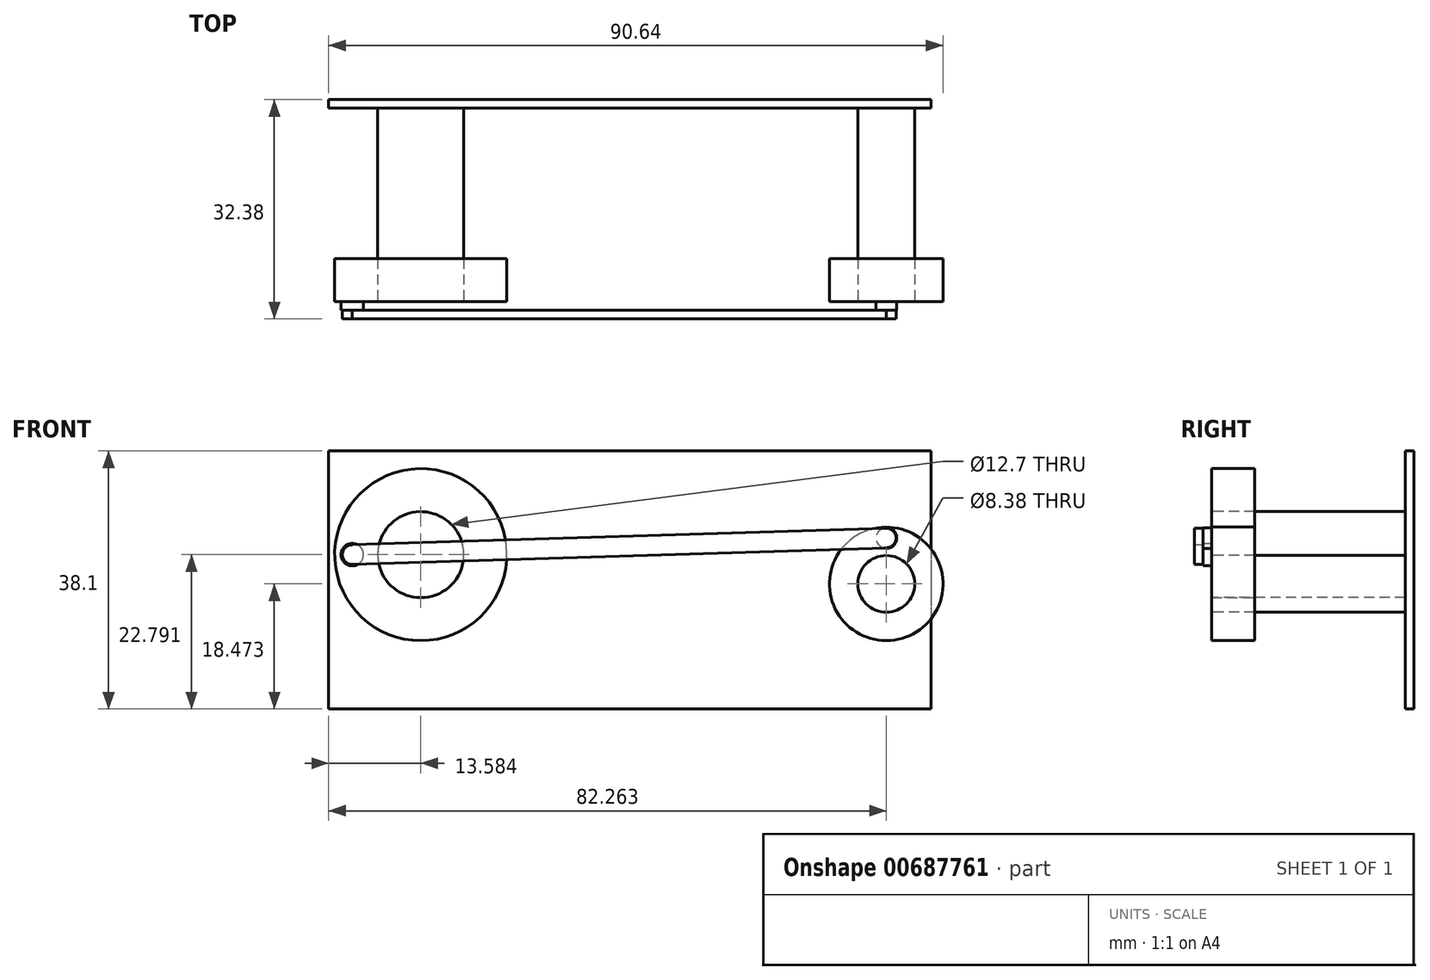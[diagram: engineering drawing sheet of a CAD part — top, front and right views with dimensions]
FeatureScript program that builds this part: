
annotation { "Feature Type Name" : "Feature", "Feature Type Description" : "" }
export const myFeature = defineFeature(function(context is Context, id is Id, definition is map)
    precondition{}
    {
        {
            var Q0;
            Q0=qCreatedBy(makeId("Front.planeOp"),FACE);
            var sketch = newSketch(context, id + "F0", { "sketchPlane" : qUnion([Q0])});
            skCircle(sketch, "E0", {"center": v(-75.94, -5.97) * mm, "radius": 12.7 * mm});
            skCircle(sketch, "E1", {"center": v(-7.26, -10.29) * mm, "radius": 8.38 * mm});
            skCircle(sketch, "E2", {"center": v(-75.94, -5.97) * mm, "radius": 6.35 * mm});
            skCircle(sketch, "E3", {"center": v(-7.26, -10.29) * mm, "radius": 4.2 * mm});
            skSolve(sketch);
        }
        {
            var Q0;
            Q0=makeQuery(id+"F0.imprint","IMPRINT",FACE,{"disambiguationData":[TD([[makeQuery(id+"F0.imprint","IMPRINT",EDGE,{"derivedFrom":sQuery(id+"F0.wireOp",EDGE,"E0")}),1.0]])]});
            var Q1;
            Q1=makeQuery(id+"F0.imprint","IMPRINT",FACE,{"disambiguationData":[TD([[makeQuery(id+"F0.imprint","IMPRINT",EDGE,{"derivedFrom":sQuery(id+"F0.wireOp",EDGE,"E1")}),1.0]])]});
            extrude(context, id + "F1", {"entities" : qUnion([Q0, Q1]), "endBound" : BoundingType.SYMMETRIC, "depth" : 6.35 * mm, "offsetDistance" : 25.4 * mm});
        }
        {
            var Q0;
            Q0=makeQuery(id+"F0.imprint","IMPRINT",FACE,{"disambiguationData":[TD([[makeQuery(id+"F0.imprint","IMPRINT",EDGE,{"derivedFrom":sQuery(id+"F0.wireOp",EDGE,"E2")}),1.0]])]});
            var Q1;
            Q1=makeQuery(id+"F0.imprint","IMPRINT",FACE,{"disambiguationData":[TD([[makeQuery(id+"F0.imprint","IMPRINT",EDGE,{"derivedFrom":sQuery(id+"F0.wireOp",EDGE,"E3")}),1.0]])]});
            var Q2;
            Q2=makeQuery(id+"F1.opExtrude","CAP_FACE",FACE,{"disambiguationData":[OSD([sQuery(id+"F0.wireOp",EDGE,"E0"),sQuery(id+"F0.wireOp",EDGE,"E2")])],"isStart":false});
            extrude(context, id + "F2", {"entities" : qUnion([Q0, Q1]), "oppositeDirection" : true, "depth" : 25.4 * mm, "offsetDistance" : 25.4 * mm, "hasSecondDirection" : true, "secondDirectionBound" : SecondDirectionBoundingType.UP_TO_SURFACE, "secondDirectionOppositeDirection" : false, "secondDirectionDepth" : 25.4 * mm, "secondDirectionBoundEntityFace" : qUnion([Q2])});
        }
        {
            var Q0;
            Q0=makeQuery(id+"F2.opExtrude","CAP_FACE",FACE,{"disambiguationData":[OSD([sQuery(id+"F0.wireOp",EDGE,"E3")])],"isStart":false});
            var sketch = newSketch(context, id + "F3", { "sketchPlane" : qUnion([Q0])});
            skLineSegment(sketch, "E4.bottom", {"start": v(0.62, 9.34) * mm, "end": v(89.52, 9.34) * mm});
            skLineSegment(sketch, "E4.top", {"start": v(0.62, -28.76) * mm, "end": v(89.52, -28.76) * mm});
            skLineSegment(sketch, "E4.left", {"start": v(0.62, 9.34) * mm, "end": v(0.62, -28.76) * mm});
            skLineSegment(sketch, "E4.right", {"start": v(89.52, 9.34) * mm, "end": v(89.52, -28.76) * mm});
            skSolve(sketch);
        }
        {
            var Q0;
            Q0=makeQuery(id+"F3.imprint","IMPRINT",FACE,{"disambiguationData":[TD([[makeQuery(id+"F3.imprint","IMPRINT",EDGE,{"derivedFrom":sQuery(id+"F3.wireOp",EDGE,"E4.bottom")}),-1.0]])]});
            var Q1;
            Q1=makeQuery(id+"F3.imprint","IMPRINT",FACE,{"disambiguationData":[TD([[makeQuery(id+"F3.imprint","IMPRINT",EDGE,{"derivedFrom":makeQuery(id+"F2.opExtrude","CAP_EDGE",EDGE,{"disambiguationData":[OSD([sQuery(id+"F0.wireOp",EDGE,"E3")])],"isStart":false})}),-1.0]])]});
            extrude(context, id + "F4", {"entities" : qUnion([Q0, Q1]), "operationType" : NewBodyOperationType.ADD, "depth" : 1.27 * mm, "offsetDistance" : 25.4 * mm});
        }
        {
            var Q0;
            Q0=makeQuery(id+"F1.opExtrude","CAP_FACE",FACE,{"disambiguationData":[OSD([sQuery(id+"F0.wireOp",EDGE,"E0")])],"isStart":false});
            var sketch = newSketch(context, id + "F5", { "sketchPlane" : qUnion([Q0])});
            skPoint(sketch, "E5", {"position": v(-75.94, -5.97) * mm});
            skCircle(sketch, "E6", {"center": v(-86.04, -5.97) * mm, "radius": 1.46 * mm});
            skPoint(sketch, "E7", {"position": v(-7.22, -10.29) * mm});
            skCircle(sketch, "E8", {"center": v(-7.22, -3.5) * mm, "radius": 1.46 * mm});
            skCircle(sketch, "E9", {"center": v(-86.04, -5.97) * mm, "radius": 1.65 * mm});
            skCircle(sketch, "E10", {"center": v(-7.22, -3.5) * mm, "radius": 1.52 * mm});
            skSolve(sketch);
        }
        {
            var Q0;
            Q0=makeQuery(id+"F5.imprint","IMPRINT",FACE,{"disambiguationData":[TD([[makeQuery(id+"F5.imprint","IMPRINT",EDGE,{"derivedFrom":sQuery(id+"F5.wireOp",EDGE,"E6")}),1.0]])]});
            var Q1;
            Q1=makeQuery(id+"F5.imprint","IMPRINT",FACE,{"disambiguationData":[TD([[makeQuery(id+"F5.imprint","IMPRINT",EDGE,{"derivedFrom":sQuery(id+"F5.wireOp",EDGE,"E8")}),1.0]])]});
            extrude(context, id + "F6", {"entities" : qUnion([Q0, Q1]), "depth" : 1.27 * mm, "offsetDistance" : 25.4 * mm});
        }
        {
            var Q0;
            Q0=makeQuery(id+"F6.opExtrude","CAP_FACE",FACE,{"disambiguationData":[OSD([sQuery(id+"F5.wireOp",EDGE,"E6")])],"isStart":false});
            var sketch = newSketch(context, id + "F7", { "sketchPlane" : qUnion([Q0])});
            skPoint(sketch, "E11", {"position": v(-86.04, -5.97) * mm});
            skArc(sketch, "E12", {"start": v(-86.04, -4.5) * mm, "mid": v(-87.51, -5.97) * mm, "end": v(-86.04, -7.43) * mm});
            skLineSegment(sketch, "E13", {"start": v(-86.04, -4.5) * mm, "end": v(-7.23, -2.05) * mm});
            skLineSegment(sketch, "E14", {"start": v(-86.04, -7.43) * mm, "end": v(-7.23, -4.97) * mm});
            skArc(sketch, "E15", {"start": v(-7.23, -4.97) * mm, "mid": v(-5.8, -3.5) * mm, "end": v(-7.23, -2.05) * mm});
            skSolve(sketch);
        }
        {
            var Q0;
            Q0=makeQuery(id+"F5.imprint","IMPRINT",FACE,{"disambiguationData":[TD([[makeQuery(id+"F5.imprint","IMPRINT",EDGE,{"derivedFrom":sQuery(id+"F5.wireOp",EDGE,"E6")}),-1.0]])]});
            extrude(context, id + "F8", {"entities" : qUnion([Q0]), "operationType" : NewBodyOperationType.ADD, "depth" : 1.27 * mm, "offsetDistance" : 25.4 * mm});
        }
        {
            var Q0;
            Q0=makeQuery(id+"F5.imprint","IMPRINT",FACE,{"disambiguationData":[TD([[makeQuery(id+"F5.imprint","IMPRINT",EDGE,{"derivedFrom":sQuery(id+"F5.wireOp",EDGE,"E8")}),-1.0]])]});
            extrude(context, id + "F9", {"entities" : qUnion([Q0]), "operationType" : NewBodyOperationType.ADD, "depth" : 1.27 * mm, "offsetDistance" : 25.4 * mm});
        }
        {
            var Q0;
            {var subQ0=sQuery(id+"F7.wireOp",EDGE,"E13");Q0=makeQuery(id+"F7.imprint","IMPRINT",FACE,{"disambiguationData":[TD([[makeQuery(id+"F7.imprint","IMPRINT",EDGE,{"derivedFrom":subQ0}),-1.0]])]});}
            var Q1;
            {var subQ0=sQuery(id+"F7.wireOp",EDGE,"E14");var subQ2=makeQuery(id+"F6.opExtrude","CAP_EDGE",EDGE,{"disambiguationData":[OSD([sQuery(id+"F5.wireOp",EDGE,"E6")])],"isStart":false});var subQ4=makeQuery(id+"F7.imprint","INTERSECT",VERTEX,{"derivedFrom":[subQ2,subQ0]});Q1=makeQuery(id+"F7.imprint","IMPRINT",FACE,{"disambiguationData":[TD([[makeQuery(id+"F7.imprint","IMPRINT",EDGE,{"disambiguationData":[TD([[subQ4,1.0]])],"derivedFrom":subQ0}),1.0]])]});}
            extrude(context, id + "F10", {"entities" : qUnion([Q0, Q1]), "operationType" : NewBodyOperationType.ADD, "depth" : 1.27 * mm, "offsetDistance" : 25.4 * mm});
        }
    });
